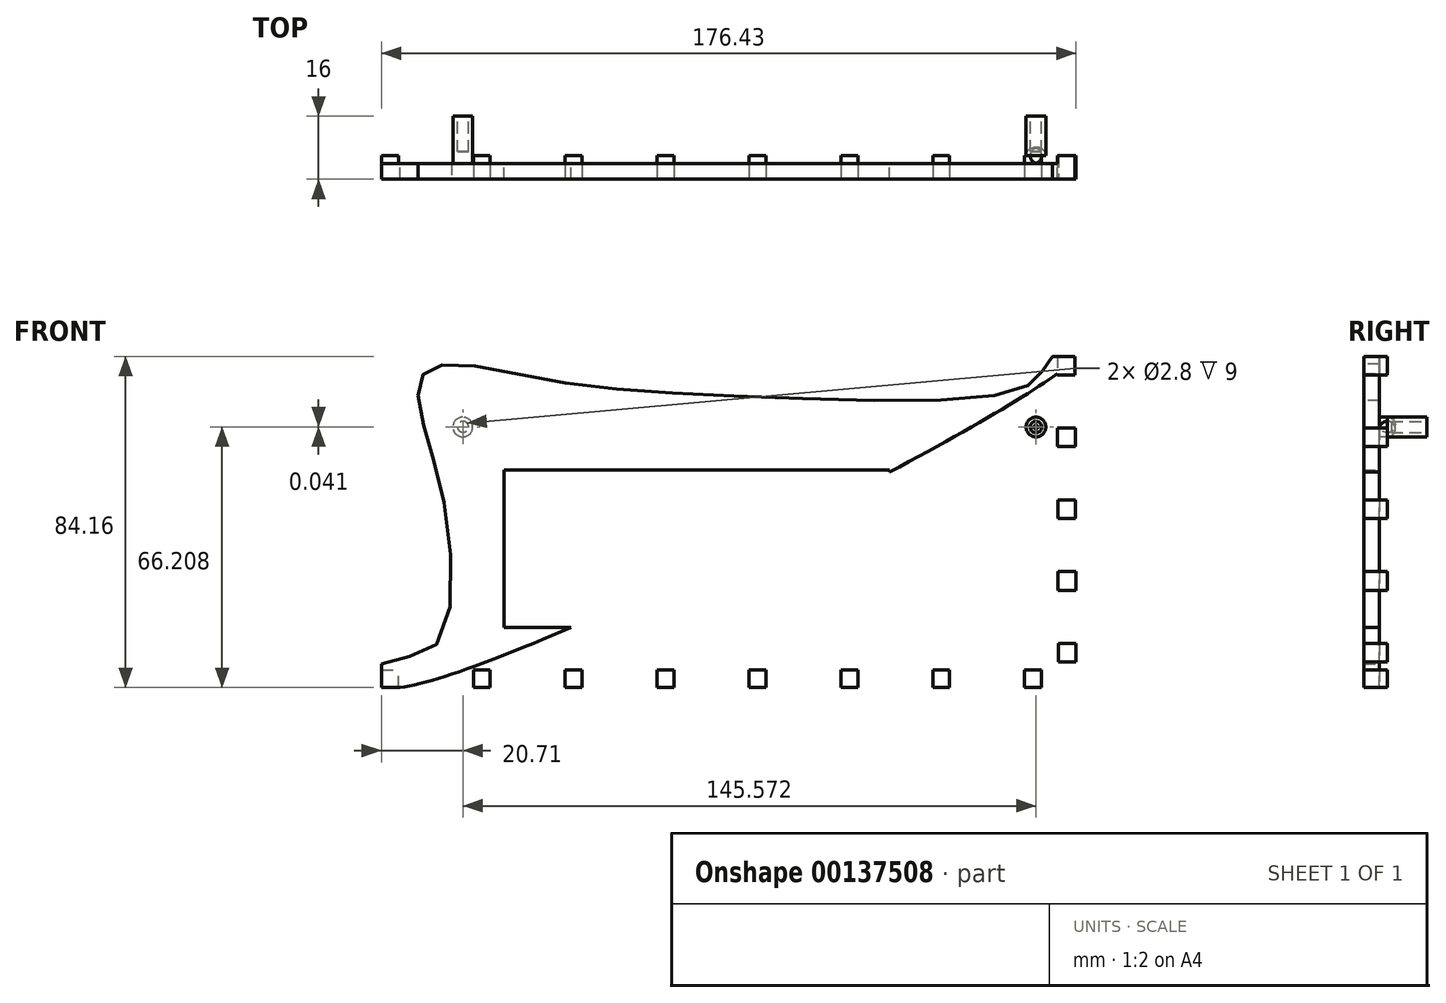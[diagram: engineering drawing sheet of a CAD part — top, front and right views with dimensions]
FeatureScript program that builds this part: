
annotation { "Feature Type Name" : "Feature", "Feature Type Description" : "" }
export const myFeature = defineFeature(function(context is Context, id is Id, definition is map)
    precondition{}
    {
        {
            var Q0;
            Q0=qCreatedBy(makeId("Front.planeOp"),FACE);
            var sketch = newSketch(context, id + "F0", { "sketchPlane" : qUnion([Q0])});
            skLineSegment(sketch, "E0.bottom", {"start": v(-77.31, 21.96) * mm, "end": v(72.69, 21.96) * mm, "construction": true});
            skLineSegment(sketch, "E0.top", {"start": v(-77.31, -41.04) * mm, "end": v(72.69, -41.04) * mm, "construction": true});
            skLineSegment(sketch, "E0.left", {"start": v(-77.31, 21.96) * mm, "end": v(-77.31, -41.04) * mm, "construction": true});
            skLineSegment(sketch, "E0.right", {"start": v(72.69, 21.96) * mm, "end": v(72.69, -41.04) * mm, "construction": true});
            skLineSegment(sketch, "E1", {"start": v(-95.43, -46.36) * mm, "end": v(-95.43, -40.35) * mm});
            skLineSegment(sketch, "E2", {"start": v(80.76, 37.8) * mm, "end": v(75.04, 37.8) * mm});
            skFitSpline(sketch, "E3", {"points": [v(-95.43, -40.35) * mm, v(-82.26, -36.25) * mm, v(-78.93, -2.99) * mm, v(-85.2, 22.25) * mm, v(-85.4, 32.43) * mm, v(-78.74, 35.75) * mm, v(-51.35, 31.45) * mm, v(0, 27.48) * mm, v(63.48, 28.43) * mm, v(72.2, 33.55) * mm, v(75.04, 37.8) * mm, v(80.76, 37.8) * mm, v(-95.43, -46.36) * mm, v(-95.43, -40.35) * mm]});
            skLineSegment(sketch, "E4.bottom", {"start": v(-64.31, 8.96) * mm, "end": v(33.69, 8.96) * mm});
            skLineSegment(sketch, "E4.top", {"start": v(-64.31, -31.04) * mm, "end": v(33.69, -31.04) * mm});
            skLineSegment(sketch, "E4.left", {"start": v(-64.31, 8.96) * mm, "end": v(-64.31, -31.04) * mm});
            skLineSegment(sketch, "E4.right", {"start": v(33.69, 8.96) * mm, "end": v(33.69, -31.04) * mm});
            skCircle(sketch, "E5", {"center": v(59.69, -7.04) * mm, "radius": 4.55 * mm});
            skCircle(sketch, "E6", {"center": v(59.69, -26.04) * mm, "radius": 2.98 * mm});
            skLineSegment(sketch, "E7", {"start": v(72.81, -46.36) * mm, "end": v(72.81, -40.54) * mm});
            skLineSegment(sketch, "E8", {"start": v(72.81, -40.54) * mm, "end": v(80.76, -40.54) * mm});
            skLineSegment(sketch, "E9", {"start": v(-95.43, -46.36) * mm, "end": v(72.81, -46.36) * mm});
            skLineSegment(sketch, "E10", {"start": v(80.76, 37.8) * mm, "end": v(80.76, -40.54) * mm});
            skSolve(sketch);
        }
        {
            var Q0;
            {var subQ0=sQuery(id+"F0.wireOp",EDGE,"E1");Q0=makeQuery(id+"F0.imprint","IMPRINT",FACE,{"disambiguationData":[TD([[makeQuery(id+"F0.imprint","IMPRINT",EDGE,{"derivedFrom":subQ0}),-1.0]])]});}
            extrude(context, id + "F1", {"entities" : qUnion([Q0]), "depth" : 4 * mm});
        }
        {
            var Q0;
            Q0=makeQuery(id+"F1.opExtrude","CAP_FACE",FACE,{"disambiguationData":[OSD([sQuery(id+"F0.wireOp",EDGE,"KkOOTngl-gOGY-si4M-3crp-3VL3Vou1fvHf"),sQuery(id+"F0.wireOp",EDGE,"FOtoh2e2-dB42-D3HZ-a7s3-6A5ojptzeBmU"),sQuery(id+"F0.wireOp",EDGE,"E1"),sQuery(id+"F0.wireOp",EDGE,"E2"),sQuery(id+"F0.wireOp",EDGE,"E3"),sQuery(id+"F0.wireOp",EDGE,"E4.bottom"),sQuery(id+"F0.wireOp",EDGE,"E4.top"),sQuery(id+"F0.wireOp",EDGE,"E4.left"),sQuery(id+"F0.wireOp",EDGE,"E4.right"),sQuery(id+"F0.wireOp",EDGE,"E5"),sQuery(id+"F0.wireOp",EDGE,"E6"),sQuery(id+"F0.wireOp",EDGE,"Dp8yctgh-aOOT-2nYt-riCS-tyILgEhAp9Hk"),sQuery(id+"F0.wireOp",EDGE,"Cd0YMjuJ-as3f-gzYX-xIN0-BSwLhn0KXe4p")])],"isStart":false});
            var sketch = newSketch(context, id + "F2", { "sketchPlane" : qUnion([Q0])});
            skLineSegment(sketch, "E11.bottom", {"start": v(-95.43, -46.36) * mm, "end": v(-91.12, -46.36) * mm});
            skLineSegment(sketch, "E11.top", {"start": v(-95.43, -41.86) * mm, "end": v(-91.12, -41.86) * mm});
            skLineSegment(sketch, "E11.left", {"start": v(-95.43, -46.36) * mm, "end": v(-95.43, -41.86) * mm});
            skLineSegment(sketch, "E11.right", {"start": v(-91.12, -46.36) * mm, "end": v(-91.12, -41.86) * mm});
            skLineSegment(sketch, "E12.1.0.0", {"start": v(-67.78, -46.36) * mm, "end": v(-67.78, -41.86) * mm});
            skLineSegment(sketch, "E12.1.0.1", {"start": v(-72.09, -46.36) * mm, "end": v(-72.09, -41.86) * mm});
            skLineSegment(sketch, "E12.1.0.2", {"start": v(-72.09, -41.86) * mm, "end": v(-67.78, -41.86) * mm});
            skLineSegment(sketch, "E12.1.0.3", {"start": v(-72.09, -46.36) * mm, "end": v(-67.78, -46.36) * mm});
            skLineSegment(sketch, "E12.2.0.0", {"start": v(-44.44, -46.36) * mm, "end": v(-44.44, -41.86) * mm});
            skLineSegment(sketch, "E12.2.0.1", {"start": v(-48.74, -46.36) * mm, "end": v(-48.74, -41.86) * mm});
            skLineSegment(sketch, "E12.2.0.2", {"start": v(-48.74, -41.86) * mm, "end": v(-44.44, -41.86) * mm});
            skLineSegment(sketch, "E12.2.0.3", {"start": v(-48.74, -46.36) * mm, "end": v(-44.44, -46.36) * mm});
            skLineSegment(sketch, "E12.3.0.0", {"start": v(-21.1, -46.36) * mm, "end": v(-21.1, -41.86) * mm});
            skLineSegment(sketch, "E12.3.0.1", {"start": v(-25.4, -46.36) * mm, "end": v(-25.4, -41.86) * mm});
            skLineSegment(sketch, "E12.3.0.2", {"start": v(-25.4, -41.86) * mm, "end": v(-21.1, -41.86) * mm});
            skLineSegment(sketch, "E12.3.0.3", {"start": v(-25.4, -46.36) * mm, "end": v(-21.1, -46.36) * mm});
            skLineSegment(sketch, "E12.4.0.0", {"start": v(2.24, -46.36) * mm, "end": v(2.24, -41.86) * mm});
            skLineSegment(sketch, "E12.4.0.1", {"start": v(-2.06, -46.36) * mm, "end": v(-2.06, -41.86) * mm});
            skLineSegment(sketch, "E12.4.0.2", {"start": v(-2.06, -41.86) * mm, "end": v(2.24, -41.86) * mm});
            skLineSegment(sketch, "E12.4.0.3", {"start": v(-2.06, -46.36) * mm, "end": v(2.24, -46.36) * mm});
            skLineSegment(sketch, "E12.5.0.0", {"start": v(25.59, -46.36) * mm, "end": v(25.59, -41.86) * mm});
            skLineSegment(sketch, "E12.5.0.1", {"start": v(21.28, -46.36) * mm, "end": v(21.28, -41.86) * mm});
            skLineSegment(sketch, "E12.5.0.2", {"start": v(21.28, -41.86) * mm, "end": v(25.59, -41.86) * mm});
            skLineSegment(sketch, "E12.5.0.3", {"start": v(21.28, -46.36) * mm, "end": v(25.59, -46.36) * mm});
            skLineSegment(sketch, "E12.6.0.0", {"start": v(48.93, -46.36) * mm, "end": v(48.93, -41.86) * mm});
            skLineSegment(sketch, "E12.6.0.1", {"start": v(44.62, -46.36) * mm, "end": v(44.62, -41.86) * mm});
            skLineSegment(sketch, "E12.6.0.2", {"start": v(44.62, -41.86) * mm, "end": v(48.93, -41.86) * mm});
            skLineSegment(sketch, "E12.6.0.3", {"start": v(44.62, -46.36) * mm, "end": v(48.93, -46.36) * mm});
            skLineSegment(sketch, "E12.7.0.0", {"start": v(72.27, -46.36) * mm, "end": v(72.27, -41.86) * mm});
            skLineSegment(sketch, "E12.7.0.1", {"start": v(67.97, -46.36) * mm, "end": v(67.97, -41.86) * mm});
            skLineSegment(sketch, "E12.7.0.2", {"start": v(67.97, -41.86) * mm, "end": v(72.27, -41.86) * mm});
            skLineSegment(sketch, "E12.7.0.3", {"start": v(67.97, -46.36) * mm, "end": v(72.27, -46.36) * mm});
            skLineSegment(sketch, "E12.direction1", {"start": v(-95.43, -46.36) * mm, "end": v(-72.09, -46.36) * mm, "construction": true});
            skLineSegment(sketch, "E13.bottom", {"start": v(80.76, 37.8) * mm, "end": v(76.26, 37.8) * mm});
            skLineSegment(sketch, "E13.top", {"start": v(80.76, 33.08) * mm, "end": v(76.26, 33.08) * mm});
            skLineSegment(sketch, "E13.left", {"start": v(80.76, 37.8) * mm, "end": v(80.76, 33.08) * mm});
            skLineSegment(sketch, "E13.right", {"start": v(76.26, 37.8) * mm, "end": v(76.26, 33.08) * mm});
            skLineSegment(sketch, "E14.1.0.0", {"start": v(80.82, 19.56) * mm, "end": v(80.82, 14.84) * mm});
            skLineSegment(sketch, "E14.1.0.1", {"start": v(80.82, 14.84) * mm, "end": v(76.32, 14.84) * mm});
            skLineSegment(sketch, "E14.1.0.2", {"start": v(80.82, 19.56) * mm, "end": v(76.32, 19.56) * mm});
            skLineSegment(sketch, "E14.1.0.3", {"start": v(76.32, 19.56) * mm, "end": v(76.32, 14.84) * mm});
            skLineSegment(sketch, "E14.2.0.0", {"start": v(80.88, 1.32) * mm, "end": v(80.88, -3.4) * mm});
            skLineSegment(sketch, "E14.2.0.1", {"start": v(80.88, -3.4) * mm, "end": v(76.38, -3.4) * mm});
            skLineSegment(sketch, "E14.2.0.2", {"start": v(80.88, 1.32) * mm, "end": v(76.38, 1.32) * mm});
            skLineSegment(sketch, "E14.2.0.3", {"start": v(76.38, 1.32) * mm, "end": v(76.38, -3.4) * mm});
            skLineSegment(sketch, "E14.3.0.0", {"start": v(80.94, -16.92) * mm, "end": v(80.94, -21.64) * mm});
            skLineSegment(sketch, "E14.3.0.1", {"start": v(80.94, -21.64) * mm, "end": v(76.44, -21.64) * mm});
            skLineSegment(sketch, "E14.3.0.2", {"start": v(80.94, -16.92) * mm, "end": v(76.44, -16.92) * mm});
            skLineSegment(sketch, "E14.3.0.3", {"start": v(76.44, -16.92) * mm, "end": v(76.44, -21.64) * mm});
            skLineSegment(sketch, "E14.4.0.0", {"start": v(81, -35.16) * mm, "end": v(81, -39.88) * mm});
            skLineSegment(sketch, "E14.4.0.1", {"start": v(81, -39.88) * mm, "end": v(76.5, -39.88) * mm});
            skLineSegment(sketch, "E14.4.0.2", {"start": v(81, -35.16) * mm, "end": v(76.5, -35.16) * mm});
            skLineSegment(sketch, "E14.4.0.3", {"start": v(76.5, -35.16) * mm, "end": v(76.5, -39.88) * mm});
            skLineSegment(sketch, "E14.direction1", {"start": v(76.26, 33.08) * mm, "end": v(76.32, 14.84) * mm, "construction": true});
            skSolve(sketch);
        }
        {
            var Q0;
            Q0=qSketchRegion(id+"F2",true);
            extrude(context, id + "F3", {"entities" : qUnion([Q0]), "operationType" : NewBodyOperationType.ADD, "oppositeDirection" : true, "depth" : 6 * mm});
        }
        {
            var Q0;
            Q0=makeQuery(id+"F1.opExtrude","CAP_FACE",FACE,{"disambiguationData":[OSD([sQuery(id+"F0.wireOp",EDGE,"E1"),sQuery(id+"F0.wireOp",EDGE,"E2"),sQuery(id+"F0.wireOp",EDGE,"E3"),sQuery(id+"F0.wireOp",EDGE,"E4.bottom"),sQuery(id+"F0.wireOp",EDGE,"E4.top"),sQuery(id+"F0.wireOp",EDGE,"E4.left"),sQuery(id+"F0.wireOp",EDGE,"E4.right"),sQuery(id+"F0.wireOp",EDGE,"E5"),sQuery(id+"F0.wireOp",EDGE,"E6"),sQuery(id+"F0.wireOp",EDGE,"E7"),sQuery(id+"F0.wireOp",EDGE,"E8"),sQuery(id+"F0.wireOp",EDGE,"E9"),sQuery(id+"F0.wireOp",EDGE,"E10")])],"isStart":true});
            var sketch = newSketch(context, id + "F4", { "sketchPlane" : qUnion([Q0])});
            skCircle(sketch, "E15", {"center": v(-70.85, 19.85) * mm, "radius": 2.52 * mm});
            skCircle(sketch, "E16", {"center": v(74.76, 19.85) * mm, "radius": 2.52 * mm});
            skSolve(sketch);
        }
        {
            var Q0;
            Q0=qSketchRegion(id+"F4",true);
            extrude(context, id + "F5", {"entities" : qUnion([Q0]), "operationType" : NewBodyOperationType.ADD, "depth" : 12 * mm});
        }
        {
            var Q0;
            Q0=makeQuery(id+"F5.opExtrude","CAP_FACE",FACE,{"disambiguationData":[OSD([sQuery(id+"F4.wireOp",EDGE,"E15")])],"isStart":false});
            var sketch = newSketch(context, id + "F6", { "sketchPlane" : qUnion([Q0])});
            skCircle(sketch, "E17", {"center": v(-70.85, 19.85) * mm, "radius": 1.4 * mm});
            skCircle(sketch, "E18", {"center": v(74.72, 19.89) * mm, "radius": 1.4 * mm});
            skSolve(sketch);
        }
        {
            var Q0;
            Q0=qSketchRegion(id+"F6",true);
            extrude(context, id + "F7", {"entities" : qUnion([Q0]), "operationType" : NewBodyOperationType.REMOVE, "oppositeDirection" : true, "depth" : 9 * mm});
        }
        {
            var Q0;
            Q0=makeQuery(id+"F5.opExtrude","CAP_EDGE",EDGE,{"disambiguationData":[OSD([sQuery(id+"F4.wireOp",EDGE,"E15")])],"isStart":true});
            var Q1;
            Q1=makeQuery(id+"F5.opExtrude","CAP_EDGE",EDGE,{"disambiguationData":[OSD([sQuery(id+"F4.wireOp",EDGE,"E16")])],"isStart":true});
            fillet(context, id + "F8", {"entities" : qUnion([Q0, Q1]), "radius" : 2 * mm, "tangentPropagation" : true, "allowEdgeOverflow" : false});
        }
    });
